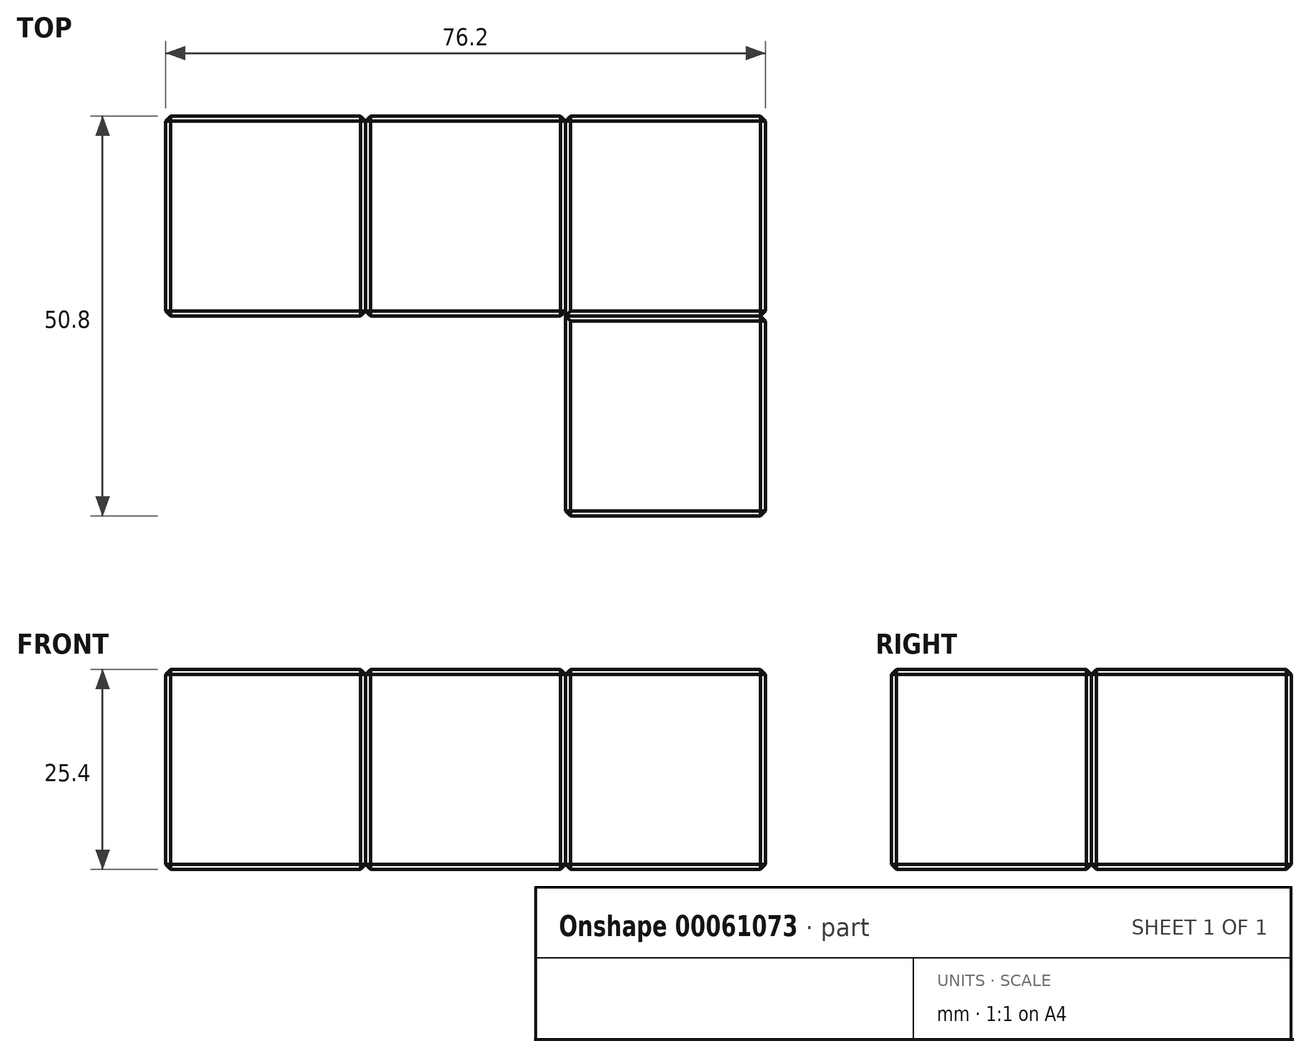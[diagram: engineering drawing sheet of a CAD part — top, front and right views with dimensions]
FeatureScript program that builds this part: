
annotation { "Feature Type Name" : "Feature", "Feature Type Description" : "" }
export const myFeature = defineFeature(function(context is Context, id is Id, definition is map)
    precondition{}
    {
        {
            var Q0;
            Q0=qCreatedBy(makeId("Top.planeOp"),FACE);
            var sketch = newSketch(context, id + "F0", { "sketchPlane" : qUnion([Q0])});
            skLineSegment(sketch, "E0.rect.bottom", {"start": v(-12.7, -12.7) * mm, "end": v(12.7, -12.7) * mm});
            skLineSegment(sketch, "E0.rect.top", {"start": v(-12.7, 12.7) * mm, "end": v(12.7, 12.7) * mm});
            skLineSegment(sketch, "E0.rect.left", {"start": v(-12.7, -12.7) * mm, "end": v(-12.7, 12.7) * mm});
            skLineSegment(sketch, "E0.rect.right", {"start": v(12.7, -12.7) * mm, "end": v(12.7, 12.7) * mm});
            skPoint(sketch, "E0.rect.middle", {"position": v(0, 0) * mm});
            skLineSegment(sketch, "E1.bottom", {"start": v(-12.7, 12.7) * mm, "end": v(-38.1, 12.7) * mm});
            skLineSegment(sketch, "E1.top", {"start": v(-12.7, -12.7) * mm, "end": v(-38.1, -12.7) * mm});
            skLineSegment(sketch, "E1.left", {"start": v(-12.7, 12.7) * mm, "end": v(-12.7, -12.7) * mm});
            skLineSegment(sketch, "E1.right", {"start": v(-38.1, 12.7) * mm, "end": v(-38.1, -12.7) * mm});
            skLineSegment(sketch, "E2.bottom", {"start": v(12.7, 12.7) * mm, "end": v(38.1, 12.7) * mm});
            skLineSegment(sketch, "E2.top", {"start": v(12.7, -12.7) * mm, "end": v(38.1, -12.7) * mm});
            skLineSegment(sketch, "E2.left", {"start": v(12.7, 12.7) * mm, "end": v(12.7, -12.7) * mm});
            skLineSegment(sketch, "E2.right", {"start": v(38.1, 12.7) * mm, "end": v(38.1, -12.7) * mm});
            skLineSegment(sketch, "E3.top", {"start": v(12.7, -38.1) * mm, "end": v(38.1, -38.1) * mm});
            skLineSegment(sketch, "E3.left", {"start": v(12.7, -12.7) * mm, "end": v(12.7, -38.1) * mm});
            skLineSegment(sketch, "E3.right", {"start": v(38.1, -12.7) * mm, "end": v(38.1, -38.1) * mm});
            skSolve(sketch);
        }
        {
            var Q0;
            Q0=makeQuery(id+"F0.imprint","IMPRINT",FACE,{"disambiguationData":[TD([[makeQuery(id+"F0.imprint","IMPRINT",EDGE,{"derivedFrom":sQuery(id+"F0.wireOp",EDGE,"E1.bottom")}),1.0]])]});
            extrude(context, id + "F1", {"entities" : qUnion([Q0]), "depth" : 25.4 * mm});
        }
        {
            var Q0;
            Q0=makeQuery(id+"F0.imprint","IMPRINT",FACE,{"disambiguationData":[TD([[makeQuery(id+"F0.imprint","IMPRINT",EDGE,{"derivedFrom":sQuery(id+"F0.wireOp",EDGE,"E2.top")}),-1.0]])]});
            extrude(context, id + "F2", {"entities" : qUnion([Q0]), "depth" : 25.4 * mm});
        }
        {
            var Q0;
            Q0=makeQuery(id+"F0.imprint","IMPRINT",FACE,{"disambiguationData":[TD([[makeQuery(id+"F0.imprint","IMPRINT",EDGE,{"derivedFrom":sQuery(id+"F0.wireOp",EDGE,"E0.rect.bottom")}),1.0]])]});
            extrude(context, id + "F3", {"entities" : qUnion([Q0]), "depth" : 25.4 * mm});
        }
        {
            var Q0;
            Q0=makeQuery(id+"F0.imprint","IMPRINT",FACE,{"disambiguationData":[TD([[makeQuery(id+"F0.imprint","IMPRINT",EDGE,{"derivedFrom":sQuery(id+"F0.wireOp",EDGE,"E2.bottom")}),-1.0]])]});
            extrude(context, id + "F4", {"entities" : qUnion([Q0]), "depth" : 25.4 * mm});
        }
        {
            var Q0;
            Q0=makeQuery(id+"F1.opExtrude","CAP_FACE",FACE,{"disambiguationData":[OSD([sQuery(id+"F0.wireOp",EDGE,"E1.bottom"),sQuery(id+"F0.wireOp",EDGE,"E1.top"),sQuery(id+"F0.wireOp",EDGE,"E1.left"),sQuery(id+"F0.wireOp",EDGE,"E1.right")])],"isStart":false});
            var Q1;
            Q1=makeQuery(id+"F3.opExtrude","CAP_FACE",FACE,{"disambiguationData":[OSD([sQuery(id+"F0.wireOp",EDGE,"E0.rect.bottom"),sQuery(id+"F0.wireOp",EDGE,"E0.rect.top"),sQuery(id+"F0.wireOp",EDGE,"E1.left"),sQuery(id+"F0.wireOp",EDGE,"E2.left")])],"isStart":false});
            var Q2;
            Q2=makeQuery(id+"F4.opExtrude","CAP_FACE",FACE,{"disambiguationData":[OSD([sQuery(id+"F0.wireOp",EDGE,"E2.bottom"),sQuery(id+"F0.wireOp",EDGE,"E2.left"),sQuery(id+"F0.wireOp",EDGE,"E2.right"),sQuery(id+"F0.wireOp",EDGE,"E2.top")])],"isStart":false});
            var Q3;
            Q3=makeQuery(id+"F2.opExtrude","CAP_FACE",FACE,{"disambiguationData":[OSD([sQuery(id+"F0.wireOp",EDGE,"E2.top"),sQuery(id+"F0.wireOp",EDGE,"E3.top"),sQuery(id+"F0.wireOp",EDGE,"E3.left"),sQuery(id+"F0.wireOp",EDGE,"E3.right")])],"isStart":false});
            var Q4;
            Q4=makeQuery(id+"F1.opExtrude","SWEPT_FACE",FACE,{"disambiguationData":[OSD([sQuery(id+"F0.wireOp",EDGE,"E1.top")])]});
            var Q5;
            Q5=makeQuery(id+"F3.opExtrude","SWEPT_FACE",FACE,{"disambiguationData":[OSD([sQuery(id+"F0.wireOp",EDGE,"E0.rect.bottom")])]});
            var Q6;
            Q6=makeQuery(id+"F2.opExtrude","SWEPT_FACE",FACE,{"disambiguationData":[OSD([sQuery(id+"F0.wireOp",EDGE,"E3.top")])]});
            var Q7;
            Q7=makeQuery(id+"F2.opExtrude","CAP_EDGE",EDGE,{"disambiguationData":[OSD([sQuery(id+"F0.wireOp",EDGE,"E3.right")])],"isStart":true});
            var Q8;
            Q8=makeQuery(id+"F4.opExtrude","CAP_EDGE",EDGE,{"disambiguationData":[OSD([sQuery(id+"F0.wireOp",EDGE,"E2.right")])],"isStart":true});
            var Q9;
            Q9=makeQuery(id+"F1.opExtrude","SWEPT_FACE",FACE,{"disambiguationData":[OSD([sQuery(id+"F0.wireOp",EDGE,"E1.bottom")])]});
            var Q10;
            Q10=makeQuery(id+"F3.opExtrude","SWEPT_FACE",FACE,{"disambiguationData":[OSD([sQuery(id+"F0.wireOp",EDGE,"E0.rect.top")])]});
            var Q11;
            Q11=makeQuery(id+"F4.opExtrude","SWEPT_FACE",FACE,{"disambiguationData":[OSD([sQuery(id+"F0.wireOp",EDGE,"E2.bottom")])]});
            var Q12;
            Q12=makeQuery(id+"F1.opExtrude","CAP_FACE",FACE,{"disambiguationData":[OSD([sQuery(id+"F0.wireOp",EDGE,"E1.bottom"),sQuery(id+"F0.wireOp",EDGE,"E1.top"),sQuery(id+"F0.wireOp",EDGE,"E1.left"),sQuery(id+"F0.wireOp",EDGE,"E1.right")])],"isStart":true});
            var Q13;
            Q13=makeQuery(id+"F3.opExtrude","CAP_FACE",FACE,{"disambiguationData":[OSD([sQuery(id+"F0.wireOp",EDGE,"E0.rect.bottom"),sQuery(id+"F0.wireOp",EDGE,"E0.rect.top"),sQuery(id+"F0.wireOp",EDGE,"E1.left"),sQuery(id+"F0.wireOp",EDGE,"E2.left")])],"isStart":true});
            var Q14;
            Q14=makeQuery(id+"F4.opExtrude","CAP_FACE",FACE,{"disambiguationData":[OSD([sQuery(id+"F0.wireOp",EDGE,"E2.bottom"),sQuery(id+"F0.wireOp",EDGE,"E2.left"),sQuery(id+"F0.wireOp",EDGE,"E2.right"),sQuery(id+"F0.wireOp",EDGE,"E2.top")])],"isStart":true});
            var Q15;
            Q15=makeQuery(id+"F2.opExtrude","CAP_FACE",FACE,{"disambiguationData":[OSD([sQuery(id+"F0.wireOp",EDGE,"E2.top"),sQuery(id+"F0.wireOp",EDGE,"E3.top"),sQuery(id+"F0.wireOp",EDGE,"E3.left"),sQuery(id+"F0.wireOp",EDGE,"E3.right")])],"isStart":true});
            var Q16;
            Q16=makeQuery(id+"F4.opExtrude","SWEPT_FACE",FACE,{"disambiguationData":[OSD([sQuery(id+"F0.wireOp",EDGE,"E2.right")])]});
            var Q17;
            Q17=makeQuery(id+"F2.opExtrude","SWEPT_FACE",FACE,{"disambiguationData":[OSD([sQuery(id+"F0.wireOp",EDGE,"E3.right")])]});
            chamfer(context, id + "F5", {"entities" : qUnion([Q0, Q1, Q2, Q3, Q4, Q5, Q6, Q7, Q8, Q9, Q10, Q11, Q12, Q13, Q14, Q15, Q16, Q17]), "width" : 0.64 * mm, "tangentPropagation" : true});
        }
    });
